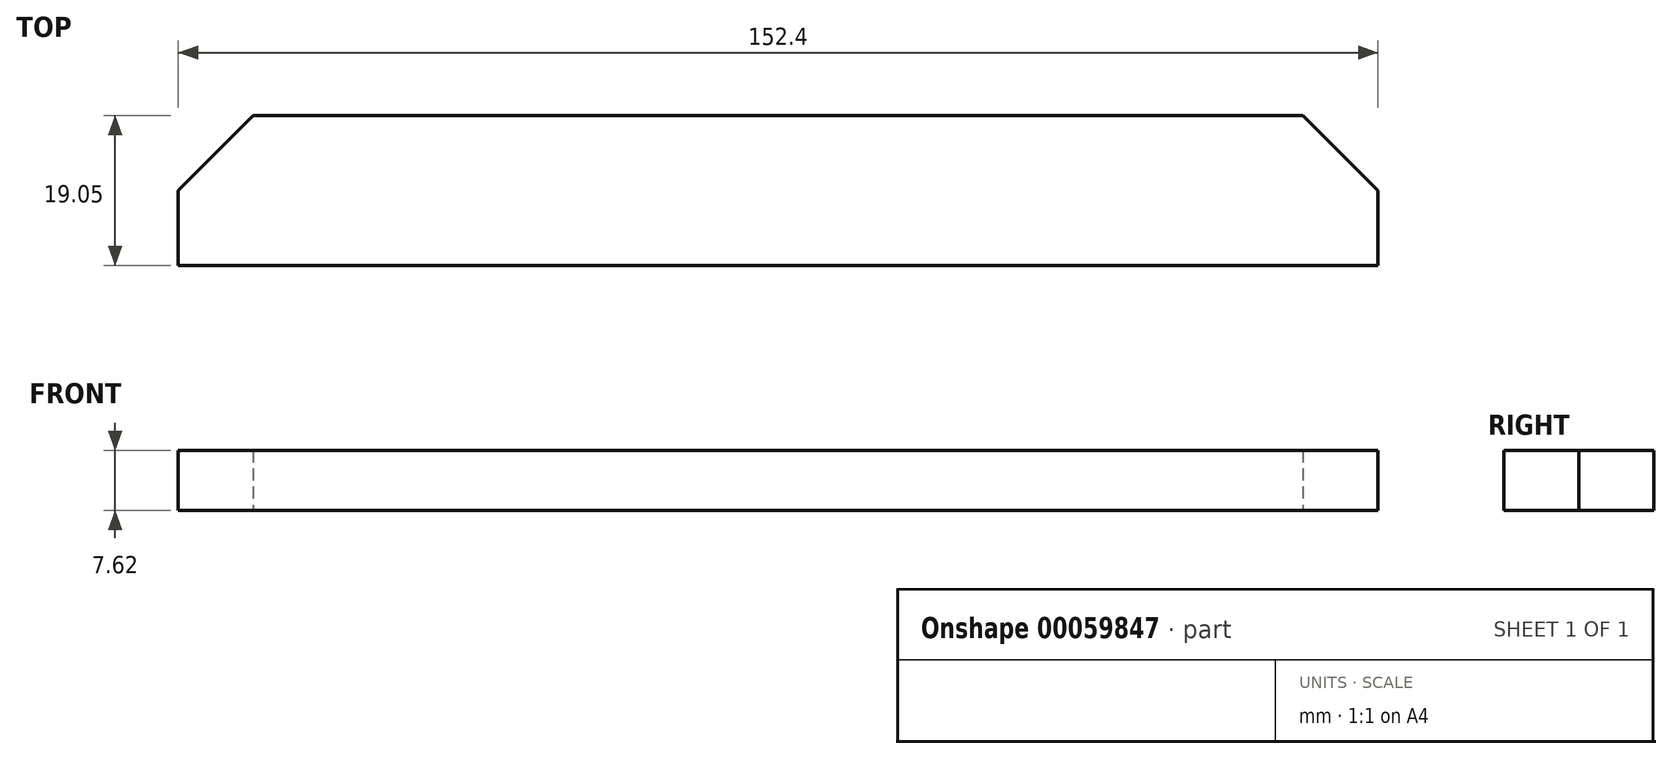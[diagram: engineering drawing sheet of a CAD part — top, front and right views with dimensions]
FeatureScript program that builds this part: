
annotation { "Feature Type Name" : "Feature", "Feature Type Description" : "" }
export const myFeature = defineFeature(function(context is Context, id is Id, definition is map)
    precondition{}
    {
        {
            var Q0;
            Q0=qCreatedBy(makeId("Top.planeOp"),FACE);
            var sketch = newSketch(context, id + "F0", { "sketchPlane" : qUnion([Q0])});
            skLineSegment(sketch, "E0", {"start": v(-76.2, 0) * mm, "end": v(76.2, 0) * mm});
            skLineSegment(sketch, "E1", {"start": v(76.2, 0) * mm, "end": v(76.2, 9.53) * mm});
            skLineSegment(sketch, "E2", {"start": v(76.2, 9.53) * mm, "end": v(66.68, 19.05) * mm});
            skLineSegment(sketch, "E3", {"start": v(66.68, 19.05) * mm, "end": v(-66.68, 19.05) * mm});
            skLineSegment(sketch, "E4", {"start": v(-66.68, 19.05) * mm, "end": v(-76.2, 9.53) * mm});
            skLineSegment(sketch, "E5", {"start": v(-76.2, 9.53) * mm, "end": v(-76.2, 0) * mm});
            skSolve(sketch);
        }
        {
            var Q0;
            Q0=makeQuery(id+"F0.imprint","IMPRINT",FACE,{"disambiguationData":[TD([[makeQuery(id+"F0.imprint","IMPRINT",EDGE,{"derivedFrom":sQuery(id+"F0.wireOp",EDGE,"E0")}),1.0]])]});
            extrude(context, id + "F1", {"entities" : qUnion([Q0]), "depth" : 7.62 * mm});
        }
    });
